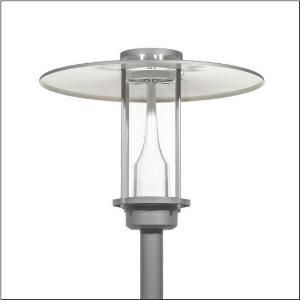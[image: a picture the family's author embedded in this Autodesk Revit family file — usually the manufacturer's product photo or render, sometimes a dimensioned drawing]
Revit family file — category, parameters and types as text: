
# Revit family: city-light_plus_iq___p1_0a_5xa5275ff14h000022_8535
name_source: partatom
category: Lighting Fixtures
units: mm (PartAtom-declared; Revit-internal decimal feet)

## family parameters
Cut with Voids When Loaded = No
Host = Face
Light Source = No
Part Type = Normal
Room Calculation Point = No
Round Connector Dimension = Use Diameter
Shared = No

## types (1)
- --- (1 x LED, 1440 lm, 10.5 W, 3000K)
    Apparent Load = 11 VA
    CIE Flux Codes = 32 61 90 96 100
    Color Rendering = 70
    Color Temperature = 3000K
    Default Elevation = 1800 mm
    Description = City-Light Plus iQ, mast luminaire, Module 540 iQ-SR, primary light control with 3 zone facetted reflector, of plastic, silver coated, highly specular, structured, primary optical cover: cover, of PMMA, transparent, light distribution: P1.0a, light emission: direct distribution, primary light characteristic: strongly asymmetric, installation type: post-top, LED, High Power LED, rated luminous flux: 1.440lm, luminous efficacy: 137lm/W, light colour: 730, colour temperature: 3000K, control gear: ECG iQ, control: Street-Remote, Auto-Match, Temp-Guard, Lumen-Switch, Night-Set, Smart-Wire, Light-Fading, Desk-Remote (wireless, voltage-free reading and setting of iQ features in the workshop via application-optimized NFC function/RFID function), optimised constant luminous flux control (CLO 2.0), presetting dimming logarithmic, mains connection: 230..240V, AC, 50/60Hz, connection cable pre-assembled, cable length: 5,5m, wiring characteristics: H07RN-F, start of lifetime: 11W, end of service life: 11W, reduction: 5W, luminaire housing, upper part, of glass-fibre reinforced polyester, coated, Siteco® metallic grey (DB 702S), diameter: 750mm, height: 590mm, spigot size: d x l = 76 x 70mm (post-top) | with reducer (optional accessory) 60 x 70mm, post-top mast mounting element, of diecast aluminium, coated, Siteco® metallic grey (DB 702S), Module 540 iQ-SR, traffic white (RAL 9016), equipment: standard, protection rating (complete): IP65, insulation class (complete): insulation class II (safety insulation), certification: CE, ENEC, VDE, packaging unit: 1 piece

Light Distribution: P1.0a
    Height = 590 mm
    Lamp = 1 x LED
    Lamp Light Flux = 1440 lm
    Lamp Power = 10.5 W
    Lamp count = 1
    Length = 750 mm
    Luminous efficacy = 137 lm/W
    Manufacturer = Siteco
    ModVariant = No
    Model = 5XA5275FF14H000022
    Number of Poles = 1
    OnlyDefault = Yes
    Power Factor = 1
    Product Name = City-Light Plus iQ | P1.0a
    Product group = mast luminaire | pylon top
    ProductGroupID = 6100
    Protection Class = Protection class II
    Protection Degree = IP 65
    RLX_Detail_Level = 1
    RLX_Emergency_Light_Flux = 0 lm
    RLX_Emergency_Type = 0
    RLX_Emergency_Type_DB = No
    RlxData = <blob elided: 51673 chars, md5=67756c6e>
    Socket = socket
    Standby Power = 0 W
    System Light Flux = 1440 lm
    System Power = 11 W
    Type Comments = factory setting: luminous flux: 100 % | dim-lin: 254 | 419 mA
    Type Image = l_1006456.jpg
    URL = http://relux.com
    VarID = @adj_110097
    Voltage = 0 V
    Weight = 0.00 kg
    Width = 0 mm  [stored 0 ft]

note: [stored X ft] marks values corroborated as IEEE doubles in the binary element streams (Revit-internal decimal feet)

## geometry (parser evidence)
native form markers: Blend x4, Sweep x11
no freeform markers — native parametric forms only
